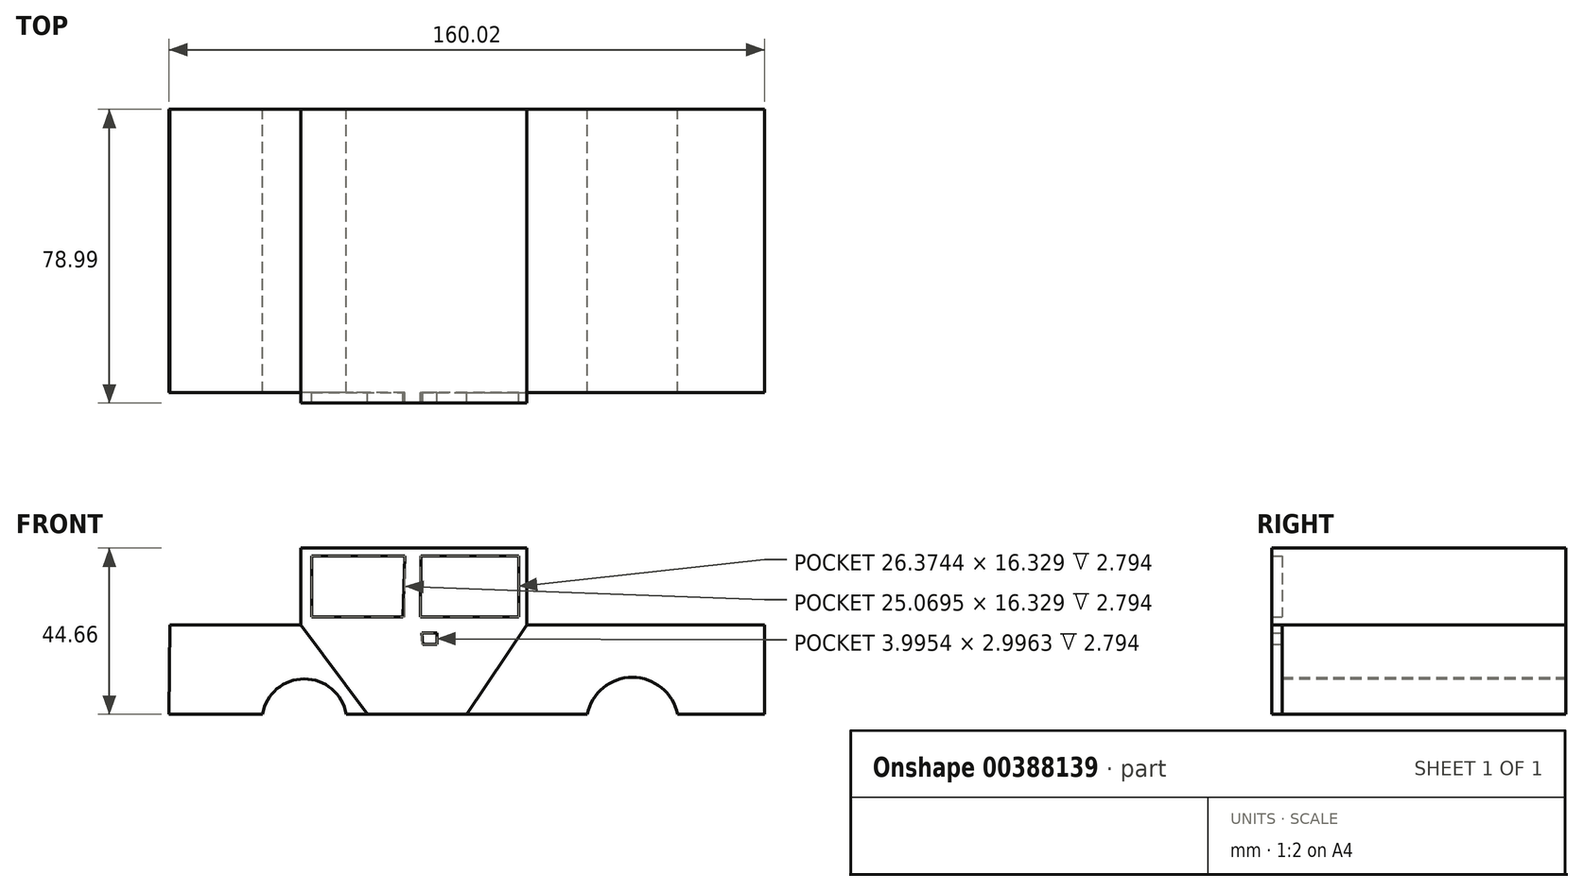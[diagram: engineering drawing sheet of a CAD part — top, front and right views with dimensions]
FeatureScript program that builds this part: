
annotation { "Feature Type Name" : "Feature", "Feature Type Description" : "" }
export const myFeature = defineFeature(function(context is Context, id is Id, definition is map)
    precondition{}
    {
        {
            var Q0;
            Q0=qCreatedBy(makeId("Front.planeOp"),FACE);
            var sketch = newSketch(context, id + "F0", { "sketchPlane" : qUnion([Q0])});
            skLineSegment(sketch, "E0", {"start": v(-128.97, 21.3) * mm, "end": v(-93.77, 21.3) * mm});
            skLineSegment(sketch, "E1", {"start": v(-93.77, 21.6) * mm, "end": v(-93.77, 42) * mm});
            skLineSegment(sketch, "E2", {"start": v(-93.77, 42) * mm, "end": v(-33.13, 42) * mm});
            skLineSegment(sketch, "E3", {"start": v(-33.13, 42) * mm, "end": v(-33.13, 21.3) * mm});
            skLineSegment(sketch, "E4", {"start": v(-33.13, 21.3) * mm, "end": v(30.76, 21.3) * mm});
            skLineSegment(sketch, "E5", {"start": v(30.76, 21.3) * mm, "end": v(30.76, -2.66) * mm});
            skLineSegment(sketch, "E6", {"start": v(30.76, -2.66) * mm, "end": v(7.4, -2.66) * mm});
            skArc(sketch, "E7", {"start": v(7.4, -2.66) * mm, "mid": v(-4.73, 7.24) * mm, "end": v(-16.86, -2.66) * mm});
            skLineSegment(sketch, "E8", {"start": v(-16.86, -2.66) * mm, "end": v(-81.64, -2.66) * mm});
            skArc(sketch, "E9", {"start": v(-81.64, -2.66) * mm, "mid": v(-92.88, 6.82) * mm, "end": v(-104.12, -2.66) * mm});
            skLineSegment(sketch, "E10", {"start": v(-104.12, -2.66) * mm, "end": v(-129.26, -2.66) * mm});
            skLineSegment(sketch, "E11", {"start": v(-129.26, -2.66) * mm, "end": v(-128.97, 21.3) * mm});
            skLineSegment(sketch, "E12", {"start": v(-93.77, 21.6) * mm, "end": v(-33.13, 21.3) * mm});
            skLineSegment(sketch, "E13", {"start": v(-63.45, 42) * mm, "end": v(-63.45, 21.45) * mm});
            skLineSegment(sketch, "E14", {"start": v(-93.77, 21.6) * mm, "end": v(-93.77, 12.98) * mm});
            skLineSegment(sketch, "E15", {"start": v(-93.77, 12.98) * mm, "end": v(-76.18, -2.66) * mm});
            skLineSegment(sketch, "E16", {"start": v(-63.45, 21.45) * mm, "end": v(-63.45, -2.66) * mm});
            skLineSegment(sketch, "E17", {"start": v(-63.45, -2.66) * mm, "end": v(-47.15, -2.66) * mm});
            skLineSegment(sketch, "E18", {"start": v(-47.15, -2.66) * mm, "end": v(-33.13, 21.3) * mm});
            skSolve(sketch);
        }
        {
            var Q0;
            {var subQ2=sQuery(id+"F0.wireOp",EDGE,"E15");Q0=makeQuery(id+"F0.imprint","IMPRINT",FACE,{"disambiguationData":[TD([[makeQuery(id+"F0.imprint","IMPRINT",EDGE,{"derivedFrom":subQ2}),1.0]])]});}
            var Q1;
            {var subQ0=sQuery(id+"F0.wireOp",EDGE,"E3");Q1=makeQuery(id+"F0.imprint","IMPRINT",FACE,{"disambiguationData":[TD([[makeQuery(id+"F0.imprint","IMPRINT",EDGE,{"derivedFrom":subQ0}),-1.0]])]});}
            var Q2;
            {var subQ0=sQuery(id+"F0.wireOp",EDGE,"E1");Q2=makeQuery(id+"F0.imprint","IMPRINT",FACE,{"disambiguationData":[TD([[makeQuery(id+"F0.imprint","IMPRINT",EDGE,{"derivedFrom":subQ0}),-1.0]])]});}
            var Q3;
            Q3=makeQuery(id+"F0.imprint","IMPRINT",FACE,{"disambiguationData":[TD([[makeQuery(id+"F0.imprint","IMPRINT",EDGE,{"derivedFrom":sQuery(id+"F0.wireOp",EDGE,"E4")}),-1.0]])]});
            var Q4;
            {var subQ3=sQuery(id+"F0.wireOp",EDGE,"E0");Q4=makeQuery(id+"F0.imprint","IMPRINT",FACE,{"disambiguationData":[TD([[makeQuery(id+"F0.imprint","IMPRINT",EDGE,{"derivedFrom":subQ3}),-1.0]])]});}
            var Q5;
            {var subQ2=sQuery(id+"F0.wireOp",EDGE,"E16");Q5=makeQuery(id+"F0.imprint","IMPRINT",FACE,{"disambiguationData":[TD([[makeQuery(id+"F0.imprint","IMPRINT",EDGE,{"derivedFrom":subQ2}),1.0]])]});}
            extrude(context, id + "F1", {"entities" : qUnion([Q0, Q1, Q2, Q3, Q4, Q5]), "depth" : 76.2 * mm});
        }
        {
            var Q0;
            Q0=makeQuery(id+"F1.opExtrude","CAP_FACE",FACE,{"disambiguationData":[OSD([sQuery(id+"F0.wireOp",EDGE,"E0"),sQuery(id+"F0.wireOp",EDGE,"E1"),sQuery(id+"F0.wireOp",EDGE,"E2"),sQuery(id+"F0.wireOp",EDGE,"E3"),sQuery(id+"F0.wireOp",EDGE,"E4"),sQuery(id+"F0.wireOp",EDGE,"E5"),sQuery(id+"F0.wireOp",EDGE,"E6"),sQuery(id+"F0.wireOp",EDGE,"E7"),sQuery(id+"F0.wireOp",EDGE,"E8"),sQuery(id+"F0.wireOp",EDGE,"E9"),sQuery(id+"F0.wireOp",EDGE,"E10"),sQuery(id+"F0.wireOp",EDGE,"E11"),sQuery(id+"F0.wireOp",EDGE,"E14"),sQuery(id+"F0.wireOp",EDGE,"E17")])],"isStart":false});
            var sketch = newSketch(context, id + "F2", { "sketchPlane" : qUnion([Q0])});
            skLineSegment(sketch, "E19", {"start": v(-93.77, 21.3) * mm, "end": v(-33.13, 21.3) * mm});
            skLineSegment(sketch, "E20", {"start": v(-63.45, 21.3) * mm, "end": v(-63.45, 42) * mm});
            skLineSegment(sketch, "E21", {"start": v(-63.45, 21.3) * mm, "end": v(-63.45, -2.66) * mm});
            skLineSegment(sketch, "E22", {"start": v(-63.45, -2.66) * mm, "end": v(-75.87, -2.66) * mm});
            skLineSegment(sketch, "E23", {"start": v(-75.87, -2.66) * mm, "end": v(-93.77, 21.3) * mm});
            skLineSegment(sketch, "E24", {"start": v(-63.45, -2.66) * mm, "end": v(-49.25, -2.66) * mm});
            skLineSegment(sketch, "E25", {"start": v(-49.25, -2.66) * mm, "end": v(-33.13, 21.3) * mm});
            skLineSegment(sketch, "E26", {"start": v(-61.09, 16.18) * mm, "end": v(-57.3, 16.18) * mm});
            skLineSegment(sketch, "E27", {"start": v(-57.3, 16.18) * mm, "end": v(-57.3, 19.18) * mm});
            skLineSegment(sketch, "E28", {"start": v(-57.3, 19.18) * mm, "end": v(-61.29, 19.18) * mm});
            skLineSegment(sketch, "E29", {"start": v(-61.29, 19.18) * mm, "end": v(-61.09, 16.18) * mm});
            skLineSegment(sketch, "E30", {"start": v(-61.68, 23.54) * mm, "end": v(-35.3, 23.54) * mm});
            skLineSegment(sketch, "E31", {"start": v(-35.3, 23.54) * mm, "end": v(-35.3, 39.87) * mm});
            skLineSegment(sketch, "E32", {"start": v(-35.3, 39.87) * mm, "end": v(-61.54, 39.87) * mm});
            skLineSegment(sketch, "E33", {"start": v(-61.54, 39.87) * mm, "end": v(-61.68, 23.54) * mm});
            skLineSegment(sketch, "E34", {"start": v(-65.86, 39.87) * mm, "end": v(-90.93, 39.87) * mm});
            skLineSegment(sketch, "E35", {"start": v(-90.93, 39.87) * mm, "end": v(-90.93, 23.54) * mm});
            skLineSegment(sketch, "E36", {"start": v(-90.93, 23.54) * mm, "end": v(-66.41, 23.54) * mm});
            skLineSegment(sketch, "E37", {"start": v(-66.41, 23.54) * mm, "end": v(-65.86, 39.87) * mm});
            skSolve(sketch);
        }
        {
            var Q0;
            Q0=makeQuery(id+"F1.opExtrude","SWEPT_FACE",FACE,{"disambiguationData":[OSD([sQuery(id+"F0.wireOp",EDGE,"E3")])]});
            var sketch = newSketch(context, id + "F3", { "sketchPlane" : qUnion([Q0])});
            skLineSegment(sketch, "E38", {"start": v(-38.1, 42) * mm, "end": v(-38.1, 21.3) * mm});
            skSolve(sketch);
        }
        {
            var Q0;
            {var subQ0=sQuery(id+"F2.wireOp",EDGE,"E20");Q0=makeQuery(id+"F2.imprint","IMPRINT",FACE,{"disambiguationData":[TD([[makeQuery(id+"F2.imprint","IMPRINT",EDGE,{"derivedFrom":subQ0}),1.0]])]});}
            var Q1;
            {var subQ0=sQuery(id+"F2.wireOp",EDGE,"E20");Q1=makeQuery(id+"F2.imprint","IMPRINT",FACE,{"disambiguationData":[TD([[makeQuery(id+"F2.imprint","IMPRINT",EDGE,{"derivedFrom":subQ0}),-1.0]])]});}
            var Q2;
            {var subQ2=sQuery(id+"F2.wireOp",EDGE,"E21");Q2=makeQuery(id+"F2.imprint","IMPRINT",FACE,{"disambiguationData":[TD([[makeQuery(id+"F2.imprint","IMPRINT",EDGE,{"derivedFrom":subQ2}),-1.0]])]});}
            var Q3;
            {var subQ1=sQuery(id+"F2.wireOp",EDGE,"E21");Q3=makeQuery(id+"F2.imprint","IMPRINT",FACE,{"disambiguationData":[TD([[makeQuery(id+"F2.imprint","IMPRINT",EDGE,{"derivedFrom":subQ1}),1.0]])]});}
            extrude(context, id + "F4", {"entities" : qUnion([Q0, Q1, Q2, Q3]), "operationType" : NewBodyOperationType.ADD, "depth" : 2.8 * mm});
        }
        {
            var Q0;
            Q0=sQuery(id+"F3.wireOp",EDGE,"E38");
            extrude(context, id + "F5", {"bodyType" : ToolBodyType.SURFACE, "surfaceEntities" : qUnion([Q0]), "depth" : 2.8 * mm});
        }
    });
